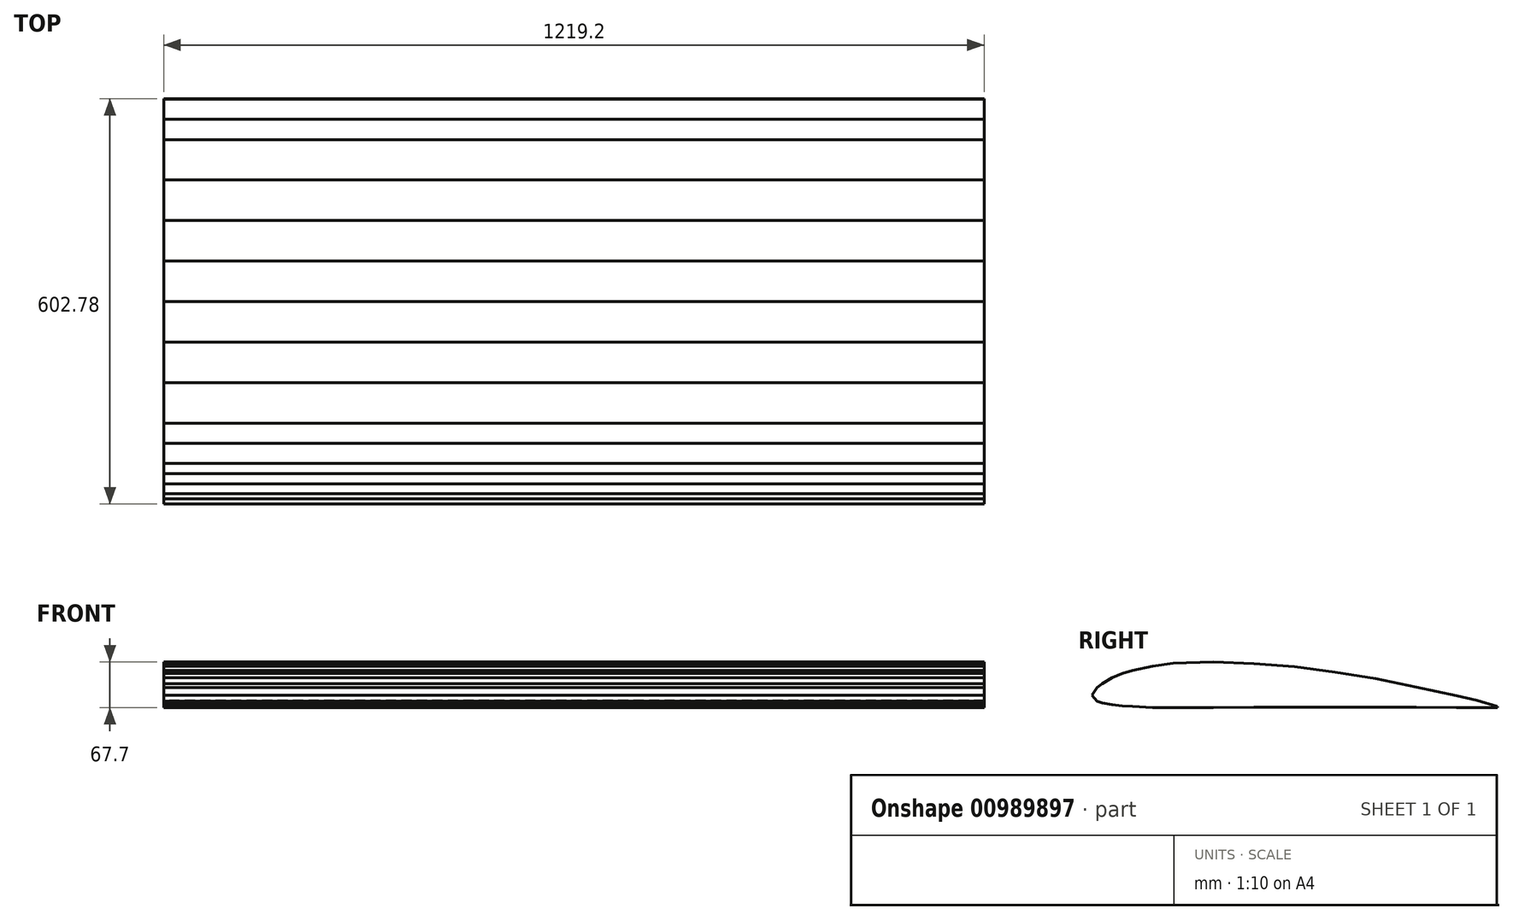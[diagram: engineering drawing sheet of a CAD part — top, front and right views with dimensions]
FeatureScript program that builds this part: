
annotation { "Feature Type Name" : "Feature", "Feature Type Description" : "" }
export const myFeature = defineFeature(function(context is Context, id is Id, definition is map)
    precondition{}
    {
        {
            var Q0;
            Q0=qCreatedBy(makeId("Right.planeOp"),FACE);
            var sketch = newSketch(context, id + "F0", { "sketchPlane" : qUnion([Q0])});
            skLineSegment(sketch, "E0", {"start": v(300.9, -31.8) * mm, "end": v(270.78, -23.37) * mm});
            skLineSegment(sketch, "E1", {"start": v(270.78, -23.37) * mm, "end": v(240.66, -16.02) * mm});
            skLineSegment(sketch, "E2", {"start": v(240.66, -16.02) * mm, "end": v(180.43, -3.13) * mm});
            skLineSegment(sketch, "E3", {"start": v(180.43, -3.13) * mm, "end": v(120.2, 9.03) * mm});
            skLineSegment(sketch, "E4", {"start": v(120.2, 9.03) * mm, "end": v(59.98, 18.8) * mm});
            skLineSegment(sketch, "E5", {"start": v(59.98, 18.8) * mm, "end": v(-0.25, 26.98) * mm});
            skLineSegment(sketch, "E6", {"start": v(-0.25, 26.98) * mm, "end": v(-60.48, 31.68) * mm});
            skLineSegment(sketch, "E7", {"start": v(-60.48, 31.68) * mm, "end": v(-120.7, 33.85) * mm});
            skLineSegment(sketch, "E8", {"start": v(-120.7, 33.85) * mm, "end": v(-180.94, 32.16) * mm});
            skLineSegment(sketch, "E9", {"start": v(-180.94, 32.16) * mm, "end": v(-211.05, 27.7) * mm});
            skLineSegment(sketch, "E10", {"start": v(-211.05, 27.7) * mm, "end": v(-241.16, 21.2) * mm});
            skLineSegment(sketch, "E11", {"start": v(-241.16, 21.2) * mm, "end": v(-256.22, 16.86) * mm});
            skLineSegment(sketch, "E12", {"start": v(-256.22, 16.86) * mm, "end": v(-271.28, 10.6) * mm});
            skLineSegment(sketch, "E13", {"start": v(-271.28, 10.6) * mm, "end": v(-286.34, 1.93) * mm});
            skLineSegment(sketch, "E14", {"start": v(-286.34, 1.93) * mm, "end": v(-293.86, -4.22) * mm});
            skLineSegment(sketch, "E15", {"start": v(-293.86, -4.22) * mm, "end": v(-301.4, -15.78) * mm});
            skLineSegment(sketch, "E16", {"start": v(-301.4, -15.78) * mm, "end": v(-293.86, -24.33) * mm});
            skLineSegment(sketch, "E17", {"start": v(-293.86, -24.33) * mm, "end": v(-286.34, -26.98) * mm});
            skLineSegment(sketch, "E18", {"start": v(-286.34, -26.98) * mm, "end": v(-271.28, -29.75) * mm});
            skLineSegment(sketch, "E19", {"start": v(-271.28, -29.75) * mm, "end": v(-256.22, -31.32) * mm});
            skLineSegment(sketch, "E20", {"start": v(-256.22, -31.32) * mm, "end": v(-241.16, -32.28) * mm});
            skLineSegment(sketch, "E21", {"start": v(-241.16, -32.28) * mm, "end": v(-211.05, -33.85) * mm});
            skLineSegment(sketch, "E22", {"start": v(-211.05, -33.85) * mm, "end": v(-180.94, -33.85) * mm});
            skLineSegment(sketch, "E23", {"start": v(-180.94, -33.85) * mm, "end": v(-120.7, -33.73) * mm});
            skLineSegment(sketch, "E24", {"start": v(-120.7, -33.73) * mm, "end": v(-60.48, -33.49) * mm});
            skLineSegment(sketch, "E25", {"start": v(-60.48, -33.49) * mm, "end": v(-0.25, -33.13) * mm});
            skLineSegment(sketch, "E26", {"start": v(-0.25, -33.13) * mm, "end": v(59.98, -33) * mm});
            skLineSegment(sketch, "E27", {"start": v(59.98, -33) * mm, "end": v(120.2, -33.25) * mm});
            skLineSegment(sketch, "E28", {"start": v(120.2, -33.25) * mm, "end": v(180.43, -33.37) * mm});
            skLineSegment(sketch, "E29", {"start": v(180.43, -33.37) * mm, "end": v(240.66, -33.6) * mm});
            skLineSegment(sketch, "E30", {"start": v(240.66, -33.6) * mm, "end": v(270.78, -33.73) * mm});
            skLineSegment(sketch, "E31", {"start": v(270.78, -33.73) * mm, "end": v(300.9, -33.85) * mm});
            skLineSegment(sketch, "E32", {"start": v(300.9, -33.85) * mm, "end": v(300.95, -33.84) * mm});
            skLineSegment(sketch, "E33", {"start": v(300.95, -33.84) * mm, "end": v(301.01, -33.83) * mm});
            skLineSegment(sketch, "E34", {"start": v(301.01, -33.83) * mm, "end": v(301.06, -33.8) * mm});
            skLineSegment(sketch, "E35", {"start": v(301.06, -33.8) * mm, "end": v(301.11, -33.77) * mm});
            skLineSegment(sketch, "E36", {"start": v(301.11, -33.77) * mm, "end": v(301.16, -33.73) * mm});
            skLineSegment(sketch, "E37", {"start": v(301.16, -33.73) * mm, "end": v(301.2, -33.68) * mm});
            skLineSegment(sketch, "E38", {"start": v(301.2, -33.68) * mm, "end": v(301.27, -33.56) * mm});
            skLineSegment(sketch, "E39", {"start": v(301.27, -33.56) * mm, "end": v(301.33, -33.41) * mm});
            skLineSegment(sketch, "E40", {"start": v(301.33, -33.41) * mm, "end": v(301.36, -33.25) * mm});
            skLineSegment(sketch, "E41", {"start": v(301.36, -33.25) * mm, "end": v(301.39, -33.08) * mm});
            skLineSegment(sketch, "E42", {"start": v(301.39, -33.08) * mm, "end": v(301.4, -32.9) * mm});
            skLineSegment(sketch, "E43", {"start": v(301.4, -32.9) * mm, "end": v(301.38, -32.71) * mm});
            skLineSegment(sketch, "E44", {"start": v(301.38, -32.71) * mm, "end": v(301.36, -32.53) * mm});
            skLineSegment(sketch, "E45", {"start": v(301.36, -32.53) * mm, "end": v(301.32, -32.36) * mm});
            skLineSegment(sketch, "E46", {"start": v(301.32, -32.36) * mm, "end": v(301.26, -32.2) * mm});
            skLineSegment(sketch, "E47", {"start": v(301.26, -32.2) * mm, "end": v(301.2, -32.06) * mm});
            skLineSegment(sketch, "E48", {"start": v(301.2, -32.06) * mm, "end": v(301.1, -31.94) * mm});
            skLineSegment(sketch, "E49", {"start": v(301.1, -31.94) * mm, "end": v(301.06, -31.9) * mm});
            skLineSegment(sketch, "E50", {"start": v(301.06, -31.9) * mm, "end": v(301, -31.85) * mm});
            skLineSegment(sketch, "E51", {"start": v(301, -31.85) * mm, "end": v(300.95, -31.82) * mm});
            skLineSegment(sketch, "E52", {"start": v(300.95, -31.82) * mm, "end": v(300.9, -31.8) * mm});
            skSolve(sketch);
        }
        {
            var Q0;
            Q0 = qSketchRegion(id + "F0", true);
            extrude(context, id + "F1", {"entities" : qUnion([Q0]), "endBound" : BoundingType.SYMMETRIC, "depth" : 1219.2 * mm, "offsetDistance" : 25.4 * mm});
        }
        {
            var Q0;
            Q0=makeQuery(id+"F1.opExtrude","CAP_FACE",FACE,{"disambiguationData":[OSD([sQuery(id+"F0.wireOp",EDGE,"E0"),sQuery(id+"F0.wireOp",EDGE,"E1"),sQuery(id+"F0.wireOp",EDGE,"E2"),sQuery(id+"F0.wireOp",EDGE,"E3"),sQuery(id+"F0.wireOp",EDGE,"E4"),sQuery(id+"F0.wireOp",EDGE,"E5"),sQuery(id+"F0.wireOp",EDGE,"E6"),sQuery(id+"F0.wireOp",EDGE,"E7"),sQuery(id+"F0.wireOp",EDGE,"E8"),sQuery(id+"F0.wireOp",EDGE,"E9"),sQuery(id+"F0.wireOp",EDGE,"E10"),sQuery(id+"F0.wireOp",EDGE,"E11"),sQuery(id+"F0.wireOp",EDGE,"E12"),sQuery(id+"F0.wireOp",EDGE,"E13"),sQuery(id+"F0.wireOp",EDGE,"E14"),sQuery(id+"F0.wireOp",EDGE,"E15"),sQuery(id+"F0.wireOp",EDGE,"E16"),sQuery(id+"F0.wireOp",EDGE,"E17"),sQuery(id+"F0.wireOp",EDGE,"E18"),sQuery(id+"F0.wireOp",EDGE,"E19"),sQuery(id+"F0.wireOp",EDGE,"E20"),sQuery(id+"F0.wireOp",EDGE,"E21"),sQuery(id+"F0.wireOp",EDGE,"E22"),sQuery(id+"F0.wireOp",EDGE,"E23"),sQuery(id+"F0.wireOp",EDGE,"E24"),sQuery(id+"F0.wireOp",EDGE,"E25"),sQuery(id+"F0.wireOp",EDGE,"E26"),sQuery(id+"F0.wireOp",EDGE,"E27"),sQuery(id+"F0.wireOp",EDGE,"E28"),sQuery(id+"F0.wireOp",EDGE,"E29"),sQuery(id+"F0.wireOp",EDGE,"E30"),sQuery(id+"F0.wireOp",EDGE,"E31"),sQuery(id+"F0.wireOp",EDGE,"E32"),sQuery(id+"F0.wireOp",EDGE,"E33"),sQuery(id+"F0.wireOp",EDGE,"E34"),sQuery(id+"F0.wireOp",EDGE,"E35"),sQuery(id+"F0.wireOp",EDGE,"E36"),sQuery(id+"F0.wireOp",EDGE,"E37"),sQuery(id+"F0.wireOp",EDGE,"E38"),sQuery(id+"F0.wireOp",EDGE,"E39"),sQuery(id+"F0.wireOp",EDGE,"E40"),sQuery(id+"F0.wireOp",EDGE,"E41"),sQuery(id+"F0.wireOp",EDGE,"E42"),sQuery(id+"F0.wireOp",EDGE,"E43"),sQuery(id+"F0.wireOp",EDGE,"E44"),sQuery(id+"F0.wireOp",EDGE,"E45"),sQuery(id+"F0.wireOp",EDGE,"E46"),sQuery(id+"F0.wireOp",EDGE,"E47"),sQuery(id+"F0.wireOp",EDGE,"E48"),sQuery(id+"F0.wireOp",EDGE,"E49"),sQuery(id+"F0.wireOp",EDGE,"E50"),sQuery(id+"F0.wireOp",EDGE,"E51"),sQuery(id+"F0.wireOp",EDGE,"E52")])],"isStart":true});
            cPlane(context, id + "F2", {"entities" : qUnion([Q0]), "cplaneType" : CPlaneType.OFFSET, "offset" : 99.06 * mm, "width" : 152.4 * mm, "height" : 152.4 * mm});
        }
        {
            var Q0;
            Q0=makeQuery(id+"F1.opExtrude","CAP_FACE",FACE,{"disambiguationData":[OSD([sQuery(id+"F0.wireOp",EDGE,"E0"),sQuery(id+"F0.wireOp",EDGE,"E1"),sQuery(id+"F0.wireOp",EDGE,"E2"),sQuery(id+"F0.wireOp",EDGE,"E3"),sQuery(id+"F0.wireOp",EDGE,"E4"),sQuery(id+"F0.wireOp",EDGE,"E5"),sQuery(id+"F0.wireOp",EDGE,"E6"),sQuery(id+"F0.wireOp",EDGE,"E7"),sQuery(id+"F0.wireOp",EDGE,"E8"),sQuery(id+"F0.wireOp",EDGE,"E9"),sQuery(id+"F0.wireOp",EDGE,"E10"),sQuery(id+"F0.wireOp",EDGE,"E11"),sQuery(id+"F0.wireOp",EDGE,"E12"),sQuery(id+"F0.wireOp",EDGE,"E13"),sQuery(id+"F0.wireOp",EDGE,"E14"),sQuery(id+"F0.wireOp",EDGE,"E15"),sQuery(id+"F0.wireOp",EDGE,"E16"),sQuery(id+"F0.wireOp",EDGE,"E17"),sQuery(id+"F0.wireOp",EDGE,"E18"),sQuery(id+"F0.wireOp",EDGE,"E19"),sQuery(id+"F0.wireOp",EDGE,"E20"),sQuery(id+"F0.wireOp",EDGE,"E21"),sQuery(id+"F0.wireOp",EDGE,"E22"),sQuery(id+"F0.wireOp",EDGE,"E23"),sQuery(id+"F0.wireOp",EDGE,"E24"),sQuery(id+"F0.wireOp",EDGE,"E25"),sQuery(id+"F0.wireOp",EDGE,"E26"),sQuery(id+"F0.wireOp",EDGE,"E27"),sQuery(id+"F0.wireOp",EDGE,"E28"),sQuery(id+"F0.wireOp",EDGE,"E29"),sQuery(id+"F0.wireOp",EDGE,"E30"),sQuery(id+"F0.wireOp",EDGE,"E31"),sQuery(id+"F0.wireOp",EDGE,"E32"),sQuery(id+"F0.wireOp",EDGE,"E33"),sQuery(id+"F0.wireOp",EDGE,"E34"),sQuery(id+"F0.wireOp",EDGE,"E35"),sQuery(id+"F0.wireOp",EDGE,"E36"),sQuery(id+"F0.wireOp",EDGE,"E37"),sQuery(id+"F0.wireOp",EDGE,"E38"),sQuery(id+"F0.wireOp",EDGE,"E39"),sQuery(id+"F0.wireOp",EDGE,"E40"),sQuery(id+"F0.wireOp",EDGE,"E41"),sQuery(id+"F0.wireOp",EDGE,"E42"),sQuery(id+"F0.wireOp",EDGE,"E43"),sQuery(id+"F0.wireOp",EDGE,"E44"),sQuery(id+"F0.wireOp",EDGE,"E45"),sQuery(id+"F0.wireOp",EDGE,"E46"),sQuery(id+"F0.wireOp",EDGE,"E47"),sQuery(id+"F0.wireOp",EDGE,"E48"),sQuery(id+"F0.wireOp",EDGE,"E49"),sQuery(id+"F0.wireOp",EDGE,"E50"),sQuery(id+"F0.wireOp",EDGE,"E51"),sQuery(id+"F0.wireOp",EDGE,"E52")])],"isStart":true});
            cPlane(context, id + "F3", {"entities" : qUnion([Q0]), "cplaneType" : CPlaneType.OFFSET, "offset" : 0 * mm, "width" : 152.4 * mm, "height" : 152.4 * mm});
        }
    });
